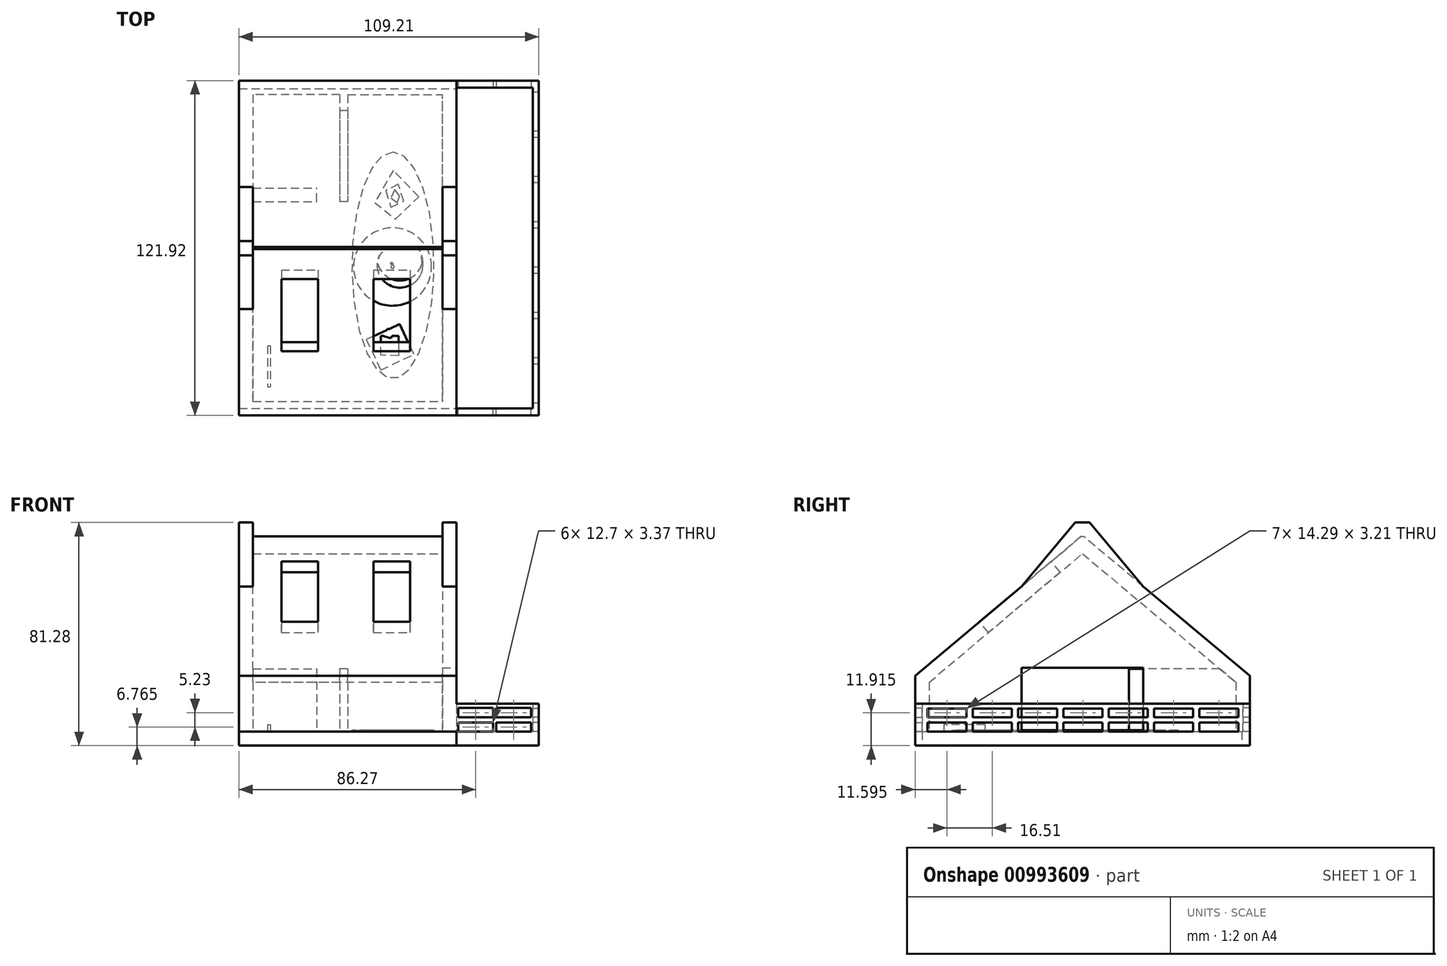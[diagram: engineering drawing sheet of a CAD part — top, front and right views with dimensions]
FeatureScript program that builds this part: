
annotation { "Feature Type Name" : "Feature", "Feature Type Description" : "" }
export const myFeature = defineFeature(function(context is Context, id is Id, definition is map)
    precondition{}
    {
        {
            var Q0;
            Q0=qCreatedBy(makeId("Top.planeOp"),FACE);
            var sketch = newSketch(context, id + "F0", { "sketchPlane" : qUnion([Q0])});
            skLineSegment(sketch, "E0.bottom", {"start": v(-69.71, 93.3) * mm, "end": v(39.5, 93.3) * mm});
            skLineSegment(sketch, "E0.top", {"start": v(-69.71, -28.62) * mm, "end": v(39.5, -28.62) * mm});
            skLineSegment(sketch, "E0.left", {"start": v(-69.71, 93.3) * mm, "end": v(-69.71, -28.62) * mm});
            skLineSegment(sketch, "E0.right", {"start": v(39.5, 93.3) * mm, "end": v(39.5, -28.62) * mm});
            skSolve(sketch);
        }
        {
            var Q0;
            Q0=makeQuery(id+"F0.imprint","IMPRINT",FACE,{"disambiguationData":[TD([[makeQuery(id+"F0.imprint","IMPRINT",EDGE,{"derivedFrom":sQuery(id+"F0.wireOp",EDGE,"E0.bottom")}),-1.0]])]});
            extrude(context, id + "F1", {"entities" : qUnion([Q0]), "depth" : 76.2 * mm, "offsetDistance" : 25.4 * mm});
        }
        {
            var Q0;
            Q0=makeQuery(id+"F1.opExtrude","CAP_FACE",FACE,{"disambiguationData":[OSD([sQuery(id+"F0.wireOp",EDGE,"E0.bottom"),sQuery(id+"F0.wireOp",EDGE,"E0.top"),sQuery(id+"F0.wireOp",EDGE,"E0.left"),sQuery(id+"F0.wireOp",EDGE,"E0.right")])],"isStart":false});
            var sketch = newSketch(context, id + "F2", { "sketchPlane" : qUnion([Q0])});
            skLineSegment(sketch, "E1.right", {"start": v(9.5, -28.62) * mm, "end": v(9.5, 93.3) * mm});
            skLineSegment(sketch, "E2.bottom", {"start": v(9.5, -28.62) * mm, "end": v(39.5, -28.62) * mm});
            skLineSegment(sketch, "E2.top", {"start": v(9.5, 93.3) * mm, "end": v(39.5, 93.3) * mm});
            skLineSegment(sketch, "E2.right", {"start": v(39.5, -28.62) * mm, "end": v(39.5, 93.3) * mm});
            skSolve(sketch);
        }
        {
            var Q0;
            Q0=qSketchRegion(id+"F2",true);
            extrude(context, id + "F3", {"entities" : qUnion([Q0]), "operationType" : NewBodyOperationType.REMOVE, "oppositeDirection" : true, "depth" : 71.12 * mm, "offsetDistance" : 25.4 * mm});
        }
        {
            var Q0;
            Q0=makeQuery(id+"F1.opExtrude","CAP_EDGE",EDGE,{"disambiguationData":[OSD([sQuery(id+"F0.wireOp",EDGE,"E0.bottom")])],"isStart":false});
            var Q1;
            Q1=makeQuery(id+"F1.opExtrude","CAP_EDGE",EDGE,{"disambiguationData":[OSD([sQuery(id+"F0.wireOp",EDGE,"E0.top")])],"isStart":false});
            chamfer(context, id + "F4", {"entities" : qUnion([Q0, Q1]), "chamferType" : ChamferType.OFFSET_ANGLE, "width" : 50.8 * mm, "oppositeDirection" : false, "angle" : 50 * degree, "tangentPropagation" : true});
        }
        {
            var Q0;
            Q0=makeQuery(id+"F3.boolean.opBoolean","COPY",FACE,{"derivedFrom":makeQuery(id+"F3.opExtrude","SWEPT_FACE",FACE,{"disambiguationData":[OSD([sQuery(id+"F2.wireOp",EDGE,"E1.right")])]})});
            var Q1;
            Q1=makeQuery(id+"F1.opExtrude","SWEPT_FACE",FACE,{"disambiguationData":[OSD([sQuery(id+"F0.wireOp",EDGE,"E0.left")])]});
            shell(context, id + "F5", {"entities" : qUnion([Q0, Q1]), "thickness" : 5.08 * mm});
        }
        {
            var Q0;
            Q0=makeQuery(id+"F5.opShell","OFFSET_FACE",FACE,{"disambiguationData":[OSD([sQuery(id+"F0.wireOp",EDGE,"E0.bottom"),sQuery(id+"F0.wireOp",EDGE,"E0.top"),sQuery(id+"F0.wireOp",EDGE,"E0.left"),sQuery(id+"F0.wireOp",EDGE,"E0.right"),sQuery(id+"F2.wireOp",EDGE,"E2.bottom"),sQuery(id+"F2.wireOp",EDGE,"E2.top"),sQuery(id+"F2.wireOp",EDGE,"E1.right"),sQuery(id+"F2.wireOp",EDGE,"E2.right")])]});
            var sketch = newSketch(context, id + "F6", { "sketchPlane" : qUnion([Q0])});
            skPoint(sketch, "E3.oppositeSnap0", {"position": v(9.5, -26.08) * mm});
            skLineSegment(sketch, "E3.bottom", {"start": v(9.5, -28.62) * mm, "end": v(39.5, -28.62) * mm});
            skLineSegment(sketch, "E3.top", {"start": v(9.5, -26.08) * mm, "end": v(39.5, -26.08) * mm});
            skLineSegment(sketch, "E3.left", {"start": v(9.5, -28.62) * mm, "end": v(9.5, -26.08) * mm});
            skLineSegment(sketch, "E3.right", {"start": v(39.5, -28.62) * mm, "end": v(39.5, -26.08) * mm});
            skPoint(sketch, "E4.oppositeSnap0", {"position": v(9.5, 90.76) * mm});
            skLineSegment(sketch, "E4.bottom", {"start": v(9.5, 93.3) * mm, "end": v(39.5, 93.3) * mm});
            skLineSegment(sketch, "E4.top", {"start": v(9.5, 90.76) * mm, "end": v(39.5, 90.76) * mm});
            skLineSegment(sketch, "E4.left", {"start": v(9.5, 93.3) * mm, "end": v(9.5, 90.76) * mm});
            skLineSegment(sketch, "E4.right", {"start": v(39.5, 93.3) * mm, "end": v(39.5, 90.76) * mm});
            skLineSegment(sketch, "E5.bottom", {"start": v(39.5, -28.62) * mm, "end": v(37.37, -28.62) * mm});
            skLineSegment(sketch, "E5.top", {"start": v(39.5, 93.3) * mm, "end": v(37.37, 93.3) * mm});
            skLineSegment(sketch, "E5.left", {"start": v(39.5, -28.62) * mm, "end": v(39.5, 93.3) * mm});
            skLineSegment(sketch, "E5.right", {"start": v(37.37, -28.62) * mm, "end": v(37.37, 93.3) * mm});
            skLineSegment(sketch, "E6.bottom", {"start": v(9.5, -23.54) * mm, "end": v(4.43, -23.54) * mm});
            skLineSegment(sketch, "E6.top", {"start": v(9.5, 88.22) * mm, "end": v(4.43, 88.22) * mm});
            skLineSegment(sketch, "E6.left", {"start": v(9.5, -23.54) * mm, "end": v(9.5, 88.22) * mm});
            skLineSegment(sketch, "E6.right", {"start": v(4.43, -23.54) * mm, "end": v(4.43, 88.22) * mm});
            skLineSegment(sketch, "E7.bottom", {"start": v(-69.71, 88.22) * mm, "end": v(-64.63, 88.22) * mm});
            skLineSegment(sketch, "E7.top", {"start": v(-69.71, -23.54) * mm, "end": v(-64.63, -23.54) * mm});
            skLineSegment(sketch, "E7.left", {"start": v(-69.71, 88.22) * mm, "end": v(-69.71, -23.54) * mm});
            skLineSegment(sketch, "E7.right", {"start": v(-64.63, 88.22) * mm, "end": v(-64.63, -23.54) * mm});
            skLineSegment(sketch, "E8.bottom", {"start": v(-30.1, 88.22) * mm, "end": v(-32.97, 88.22) * mm});
            skLineSegment(sketch, "E8.top", {"start": v(-30.1, 49.23) * mm, "end": v(-32.97, 49.23) * mm});
            skLineSegment(sketch, "E8.left", {"start": v(-30.1, 88.22) * mm, "end": v(-30.1, 49.23) * mm});
            skLineSegment(sketch, "E8.right", {"start": v(-32.97, 88.22) * mm, "end": v(-32.97, 49.23) * mm});
            skLineSegment(sketch, "E9.bottom", {"start": v(-64.63, 49.23) * mm, "end": v(-41.45, 49.23) * mm});
            skLineSegment(sketch, "E9.top", {"start": v(-64.63, 54.2) * mm, "end": v(-41.45, 54.2) * mm});
            skLineSegment(sketch, "E9.left", {"start": v(-64.63, 49.23) * mm, "end": v(-64.63, 54.2) * mm});
            skLineSegment(sketch, "E9.right", {"start": v(-41.45, 49.23) * mm, "end": v(-41.45, 54.2) * mm});
            skEllipse(sketch, "E10", {"center": v(-13.6, 26.06) * mm, "majorRadius": 41.26 * mm, "minorRadius": 14.98 * mm, "majorAxis": v(0, 1)});
            skSolve(sketch);
        }
        {
            var Q0;
            Q0=makeQuery(id+"F6.imprint","IMPRINT",FACE,{"disambiguationData":[TD([[makeQuery(id+"F6.imprint","IMPRINT",EDGE,{"derivedFrom":sQuery(id+"F6.wireOp",EDGE,"E7.bottom")}),-1.0]])]});
            var Q1;
            Q1=makeQuery(id+"F6.imprint","IMPRINT",FACE,{"disambiguationData":[TD([[makeQuery(id+"F6.imprint","IMPRINT",EDGE,{"derivedFrom":sQuery(id+"F6.wireOp",EDGE,"E6.bottom")}),1.0]])]});
            var Q2;
            Q2=qSketchRegion(id+"F9",true);
            extrude(context, id + "F7", {"entities" : qUnion([Q0, Q1, Q2]), "operationType" : NewBodyOperationType.ADD, "depth" : 76.2 * mm, "offsetDistance" : 25.4 * mm});
        }
        {
            var Q0;
            Q0=makeQuery(id+"F7.opExtrude","CAP_EDGE",EDGE,{"disambiguationData":[OSD([sQuery(id+"F6.wireOp",EDGE,"E6.top")])],"isStart":false});
            var Q1;
            Q1=makeQuery(id+"F7.opExtrude","CAP_EDGE",EDGE,{"disambiguationData":[OSD([sQuery(id+"F6.wireOp",EDGE,"E7.bottom")])],"isStart":false});
            var Q2;
            Q2=makeQuery(id+"F7.opExtrude","CAP_EDGE",EDGE,{"disambiguationData":[OSD([sQuery(id+"F6.wireOp",EDGE,"E6.bottom")])],"isStart":false});
            chamfer(context, id + "F8", {"entities" : qUnion([Q0, Q1, Q2]), "chamferType" : ChamferType.OFFSET_ANGLE, "width" : 63.5 * mm, "oppositeDirection" : false, "angle" : 40 * degree});
        }
        {
            var Q0;
            Q0=makeQuery(id+"F7.boolean.opBoolean","MERGE",FACE,{"derivedFrom":[makeQuery(id+"F1.opExtrude","SWEPT_FACE",FACE,{"disambiguationData":[OSD([sQuery(id+"F0.wireOp",EDGE,"E0.left")])]}),makeQuery(id+"F7.opExtrude","SWEPT_FACE",FACE,{"disambiguationData":[OSD([sQuery(id+"F6.wireOp",EDGE,"E7.left")])]})]});
            var sketch = newSketch(context, id + "F9", { "sketchPlane" : qUnion([Q0])});
            skLineSegment(sketch, "E11.0.0", {"start": v(-31.92, 76.2) * mm, "end": v(23.54, 29.66) * mm});
            skLineSegment(sketch, "E11.0.2", {"start": v(23.54, 29.66) * mm, "end": v(28.62, 25.4) * mm});
            skLineSegment(sketch, "E11.0.4", {"start": v(28.62, 25.4) * mm, "end": v(-10.15, 57.94) * mm});
            skLineSegment(sketch, "E11.0.6", {"start": v(-10.15, 57.94) * mm, "end": v(-31.92, 76.2) * mm});
            skLineSegment(sketch, "E12.0.0", {"start": v(-31.92, 76.2) * mm, "end": v(-10.15, 57.94) * mm});
            skLineSegment(sketch, "E12.0.1", {"start": v(-10.15, 57.94) * mm, "end": v(-29.74, 81.28) * mm});
            skLineSegment(sketch, "E12.0.2", {"start": v(-29.74, 81.28) * mm, "end": v(-34.94, 81.28) * mm});
            skLineSegment(sketch, "E12.0.3", {"start": v(-34.94, 81.28) * mm, "end": v(-54.52, 57.94) * mm});
            skLineSegment(sketch, "E12.0.4", {"start": v(-54.52, 57.94) * mm, "end": v(-32.76, 76.2) * mm});
            skLineSegment(sketch, "E12.0.5", {"start": v(-32.76, 76.2) * mm, "end": v(-31.92, 76.2) * mm});
            skLineSegment(sketch, "E13.0.1", {"start": v(-54.52, 57.94) * mm, "end": v(-93.3, 25.4) * mm});
            skLineSegment(sketch, "E13.0.2", {"start": v(-93.3, 25.4) * mm, "end": v(-93.3, 0) * mm});
            skLineSegment(sketch, "E13.0.3", {"start": v(-93.3, 0) * mm, "end": v(28.62, 0) * mm});
            skLineSegment(sketch, "E13.0.4", {"start": v(28.62, 0) * mm, "end": v(28.62, 25.4) * mm});
            skLineSegment(sketch, "E13.0.5", {"start": v(28.62, 25.4) * mm, "end": v(23.54, 29.66) * mm});
            skLineSegment(sketch, "E13.0.6", {"start": v(23.54, 29.66) * mm, "end": v(23.54, 81.28) * mm});
            skLineSegment(sketch, "E13.0.7", {"start": v(23.54, 81.28) * mm, "end": v(-34.94, 81.28) * mm});
            skSolve(sketch);
        }
        {
            var Q0;
            Q0=makeQuery(id+"F9.imprint","IMPRINT",FACE,{"disambiguationData":[TD([[makeQuery(id+"F9.imprint","IMPRINT",EDGE,{"derivedFrom":sQuery(id+"F9.wireOp",EDGE,"E11.0.4")}),-1.0]])]});
            extrude(context, id + "F10", {"entities" : qUnion([Q0]), "operationType" : NewBodyOperationType.REMOVE, "oppositeDirection" : true, "depth" : 25.4 * mm, "offsetDistance" : 25.4 * mm});
        }
        {
            var Q0;
            {var subQ0=sQuery(id+"F6.wireOp",EDGE,"E3.bottom");Q0=makeQuery(id+"F6.imprint","IMPRINT",FACE,{"disambiguationData":[TD([[makeQuery(id+"F6.imprint","IMPRINT",EDGE,{"derivedFrom":subQ0}),1.0]])]});}
            var Q1;
            {var subQ5=sQuery(id+"F6.wireOp",EDGE,"E5.bottom");Q1=makeQuery(id+"F6.imprint","IMPRINT",FACE,{"disambiguationData":[TD([[makeQuery(id+"F6.imprint","IMPRINT",EDGE,{"derivedFrom":subQ5}),1.0]])]});}
            var Q2;
            {var subQ0=sQuery(id+"F6.wireOp",EDGE,"E5.left");var subQ1=sQuery(id+"F6.wireOp",EDGE,"E3.top");var subQ2=makeQuery(id+"F6.imprint","INTERSECT",VERTEX,{"derivedFrom":[subQ1,subQ0]});Q2=makeQuery(id+"F6.imprint","IMPRINT",FACE,{"disambiguationData":[TD([[makeQuery(id+"F6.imprint","IMPRINT",EDGE,{"disambiguationData":[TD([[subQ2,1.0]])],"derivedFrom":subQ1}),1.0]])]});}
            var Q3;
            {var subQ0=sQuery(id+"F6.wireOp",EDGE,"E4.bottom");Q3=makeQuery(id+"F6.imprint","IMPRINT",FACE,{"disambiguationData":[TD([[makeQuery(id+"F6.imprint","IMPRINT",EDGE,{"derivedFrom":subQ0}),-1.0]])]});}
            var Q4;
            {var subQ5=sQuery(id+"F6.wireOp",EDGE,"E5.top");Q4=makeQuery(id+"F6.imprint","IMPRINT",FACE,{"disambiguationData":[TD([[makeQuery(id+"F6.imprint","IMPRINT",EDGE,{"derivedFrom":subQ5}),-1.0]])]});}
            extrude(context, id + "F11", {"entities" : qUnion([Q0, Q1, Q2, Q3, Q4]), "operationType" : NewBodyOperationType.ADD, "depth" : 10.16 * mm, "offsetDistance" : 25.4 * mm});
        }
        {
            var Q0;
            Q0=makeQuery(id+"F11.opExtrude","SWEPT_FACE",FACE,{"disambiguationData":[OSD([sQuery(id+"F6.wireOp",EDGE,"E5.right")])]});
            var sketch = newSketch(context, id + "F12", { "sketchPlane" : qUnion([Q0])});
            skLineSegment(sketch, "E14.bottom", {"start": v(-89.18, 5.08) * mm, "end": v(-74.89, 5.08) * mm});
            skLineSegment(sketch, "E14.top", {"start": v(-89.18, 8.45) * mm, "end": v(-74.89, 8.45) * mm});
            skLineSegment(sketch, "E14.left", {"start": v(-89.18, 5.08) * mm, "end": v(-89.18, 8.45) * mm});
            skLineSegment(sketch, "E14.right", {"start": v(-74.89, 5.08) * mm, "end": v(-74.89, 8.45) * mm});
            skLineSegment(sketch, "E15.bottom", {"start": v(-89.18, 10.31) * mm, "end": v(-74.89, 10.31) * mm});
            skLineSegment(sketch, "E15.top", {"start": v(-89.18, 13.52) * mm, "end": v(-74.89, 13.52) * mm});
            skLineSegment(sketch, "E15.left", {"start": v(-89.18, 10.31) * mm, "end": v(-89.18, 13.52) * mm});
            skLineSegment(sketch, "E15.right", {"start": v(-74.89, 10.31) * mm, "end": v(-74.89, 13.52) * mm});
            skLineSegment(sketch, "E16.1.0.0", {"start": v(-58.38, 5.08) * mm, "end": v(-58.38, 8.45) * mm});
            skLineSegment(sketch, "E16.1.0.1", {"start": v(-72.67, 5.08) * mm, "end": v(-58.38, 5.08) * mm});
            skLineSegment(sketch, "E16.1.0.2", {"start": v(-72.67, 10.31) * mm, "end": v(-72.67, 13.52) * mm});
            skLineSegment(sketch, "E16.1.0.3", {"start": v(-72.67, 10.31) * mm, "end": v(-58.38, 10.31) * mm});
            skLineSegment(sketch, "E16.1.0.4", {"start": v(-58.38, 10.31) * mm, "end": v(-58.38, 13.52) * mm});
            skLineSegment(sketch, "E16.1.0.5", {"start": v(-72.67, 8.45) * mm, "end": v(-58.38, 8.45) * mm});
            skLineSegment(sketch, "E16.1.0.6", {"start": v(-72.67, 13.52) * mm, "end": v(-58.38, 13.52) * mm});
            skLineSegment(sketch, "E16.1.0.7", {"start": v(-72.67, 5.08) * mm, "end": v(-72.67, 8.45) * mm});
            skLineSegment(sketch, "E16.2.0.0", {"start": v(-41.87, 5.08) * mm, "end": v(-41.87, 8.45) * mm});
            skLineSegment(sketch, "E16.2.0.1", {"start": v(-56.16, 5.08) * mm, "end": v(-41.87, 5.08) * mm});
            skLineSegment(sketch, "E16.2.0.2", {"start": v(-56.16, 10.31) * mm, "end": v(-56.16, 13.52) * mm});
            skLineSegment(sketch, "E16.2.0.3", {"start": v(-56.16, 10.31) * mm, "end": v(-41.87, 10.31) * mm});
            skLineSegment(sketch, "E16.2.0.4", {"start": v(-41.87, 10.31) * mm, "end": v(-41.87, 13.52) * mm});
            skLineSegment(sketch, "E16.2.0.5", {"start": v(-56.16, 8.45) * mm, "end": v(-41.87, 8.45) * mm});
            skLineSegment(sketch, "E16.2.0.6", {"start": v(-56.16, 13.52) * mm, "end": v(-41.87, 13.52) * mm});
            skLineSegment(sketch, "E16.2.0.7", {"start": v(-56.16, 5.08) * mm, "end": v(-56.16, 8.45) * mm});
            skLineSegment(sketch, "E16.3.0.0", {"start": v(-25.36, 5.08) * mm, "end": v(-25.36, 8.45) * mm});
            skLineSegment(sketch, "E16.3.0.1", {"start": v(-39.65, 5.08) * mm, "end": v(-25.36, 5.08) * mm});
            skLineSegment(sketch, "E16.3.0.2", {"start": v(-39.65, 10.31) * mm, "end": v(-39.65, 13.52) * mm});
            skLineSegment(sketch, "E16.3.0.3", {"start": v(-39.65, 10.31) * mm, "end": v(-25.36, 10.31) * mm});
            skLineSegment(sketch, "E16.3.0.4", {"start": v(-25.36, 10.31) * mm, "end": v(-25.36, 13.52) * mm});
            skLineSegment(sketch, "E16.3.0.5", {"start": v(-39.65, 8.45) * mm, "end": v(-25.36, 8.45) * mm});
            skLineSegment(sketch, "E16.3.0.6", {"start": v(-39.65, 13.52) * mm, "end": v(-25.36, 13.52) * mm});
            skLineSegment(sketch, "E16.3.0.7", {"start": v(-39.65, 5.08) * mm, "end": v(-39.65, 8.45) * mm});
            skLineSegment(sketch, "E16.4.0.0", {"start": v(-8.85, 5.08) * mm, "end": v(-8.85, 8.45) * mm});
            skLineSegment(sketch, "E16.4.0.1", {"start": v(-23.14, 5.08) * mm, "end": v(-8.85, 5.08) * mm});
            skLineSegment(sketch, "E16.4.0.2", {"start": v(-23.14, 10.31) * mm, "end": v(-23.14, 13.52) * mm});
            skLineSegment(sketch, "E16.4.0.3", {"start": v(-23.14, 10.31) * mm, "end": v(-8.85, 10.31) * mm});
            skLineSegment(sketch, "E16.4.0.4", {"start": v(-8.85, 10.31) * mm, "end": v(-8.85, 13.52) * mm});
            skLineSegment(sketch, "E16.4.0.5", {"start": v(-23.14, 8.45) * mm, "end": v(-8.85, 8.45) * mm});
            skLineSegment(sketch, "E16.4.0.6", {"start": v(-23.14, 13.52) * mm, "end": v(-8.85, 13.52) * mm});
            skLineSegment(sketch, "E16.4.0.7", {"start": v(-23.14, 5.08) * mm, "end": v(-23.14, 8.45) * mm});
            skLineSegment(sketch, "E16.5.0.0", {"start": v(7.66, 5.08) * mm, "end": v(7.66, 8.45) * mm});
            skLineSegment(sketch, "E16.5.0.1", {"start": v(-6.63, 5.08) * mm, "end": v(7.66, 5.08) * mm});
            skLineSegment(sketch, "E16.5.0.2", {"start": v(-6.63, 10.31) * mm, "end": v(-6.63, 13.52) * mm});
            skLineSegment(sketch, "E16.5.0.3", {"start": v(-6.63, 10.31) * mm, "end": v(7.66, 10.31) * mm});
            skLineSegment(sketch, "E16.5.0.4", {"start": v(7.66, 10.31) * mm, "end": v(7.66, 13.52) * mm});
            skLineSegment(sketch, "E16.5.0.5", {"start": v(-6.63, 8.45) * mm, "end": v(7.66, 8.45) * mm});
            skLineSegment(sketch, "E16.5.0.6", {"start": v(-6.63, 13.52) * mm, "end": v(7.66, 13.52) * mm});
            skLineSegment(sketch, "E16.5.0.7", {"start": v(-6.63, 5.08) * mm, "end": v(-6.63, 8.45) * mm});
            skLineSegment(sketch, "E16.6.0.0", {"start": v(24.17, 5.08) * mm, "end": v(24.17, 8.45) * mm});
            skLineSegment(sketch, "E16.6.0.1", {"start": v(9.88, 5.08) * mm, "end": v(24.17, 5.08) * mm});
            skLineSegment(sketch, "E16.6.0.2", {"start": v(9.88, 10.31) * mm, "end": v(9.88, 13.52) * mm});
            skLineSegment(sketch, "E16.6.0.3", {"start": v(9.88, 10.31) * mm, "end": v(24.17, 10.31) * mm});
            skLineSegment(sketch, "E16.6.0.4", {"start": v(24.17, 10.31) * mm, "end": v(24.17, 13.52) * mm});
            skLineSegment(sketch, "E16.6.0.5", {"start": v(9.88, 8.45) * mm, "end": v(24.17, 8.45) * mm});
            skLineSegment(sketch, "E16.6.0.6", {"start": v(9.88, 13.52) * mm, "end": v(24.17, 13.52) * mm});
            skLineSegment(sketch, "E16.6.0.7", {"start": v(9.88, 5.08) * mm, "end": v(9.88, 8.45) * mm});
            skLineSegment(sketch, "E16.direction1", {"start": v(-89.18, 5.08) * mm, "end": v(-72.67, 5.08) * mm, "construction": true});
            skSolve(sketch);
        }
        {
            var Q0;
            Q0=qSketchRegion(id+"F12",true);
            extrude(context, id + "F13", {"entities" : qUnion([Q0]), "operationType" : NewBodyOperationType.REMOVE, "oppositeDirection" : true, "depth" : 5.08 * mm, "offsetDistance" : 25.4 * mm});
        }
        {
            var Q0;
            Q0=makeQuery(id+"F11.opExtrude","SWEPT_FACE",FACE,{"disambiguationData":[OSD([sQuery(id+"F6.wireOp",EDGE,"E3.top")])]});
            var sketch = newSketch(context, id + "F14", { "sketchPlane" : qUnion([Q0])});
            skLineSegment(sketch, "E17.bottom", {"start": v(-36.75, 5.08) * mm, "end": v(-24.05, 5.08) * mm});
            skLineSegment(sketch, "E17.top", {"start": v(-36.75, 8.45) * mm, "end": v(-24.05, 8.45) * mm});
            skLineSegment(sketch, "E17.left", {"start": v(-36.75, 5.08) * mm, "end": v(-36.75, 8.45) * mm});
            skLineSegment(sketch, "E17.right", {"start": v(-24.05, 5.08) * mm, "end": v(-24.05, 8.45) * mm});
            skLineSegment(sketch, "E18.0.1.0", {"start": v(-24.05, 10.31) * mm, "end": v(-24.05, 13.68) * mm});
            skLineSegment(sketch, "E18.0.1.1", {"start": v(-36.75, 13.68) * mm, "end": v(-24.05, 13.68) * mm});
            skLineSegment(sketch, "E18.0.1.2", {"start": v(-36.75, 10.31) * mm, "end": v(-24.05, 10.31) * mm});
            skLineSegment(sketch, "E18.0.1.3", {"start": v(-36.75, 10.31) * mm, "end": v(-36.75, 13.68) * mm});
            skLineSegment(sketch, "E18.1.0.0", {"start": v(-10.23, 5.08) * mm, "end": v(-10.23, 8.45) * mm});
            skLineSegment(sketch, "E18.1.0.1", {"start": v(-22.93, 8.45) * mm, "end": v(-10.23, 8.45) * mm});
            skLineSegment(sketch, "E18.1.0.2", {"start": v(-22.93, 5.08) * mm, "end": v(-10.23, 5.08) * mm});
            skLineSegment(sketch, "E18.1.0.3", {"start": v(-22.93, 5.08) * mm, "end": v(-22.93, 8.45) * mm});
            skLineSegment(sketch, "E18.1.1.0", {"start": v(-10.23, 10.31) * mm, "end": v(-10.23, 13.68) * mm});
            skLineSegment(sketch, "E18.1.1.1", {"start": v(-22.93, 13.68) * mm, "end": v(-10.23, 13.68) * mm});
            skLineSegment(sketch, "E18.1.1.2", {"start": v(-22.93, 10.31) * mm, "end": v(-10.23, 10.31) * mm});
            skLineSegment(sketch, "E18.1.1.3", {"start": v(-22.93, 10.31) * mm, "end": v(-22.93, 13.68) * mm});
            skLineSegment(sketch, "E18.direction1", {"start": v(-36.75, 5.08) * mm, "end": v(-22.93, 5.08) * mm, "construction": true});
            skLineSegment(sketch, "E18.direction2", {"start": v(-36.75, 5.08) * mm, "end": v(-36.75, 10.31) * mm, "construction": true});
            skSolve(sketch);
        }
        {
            var Q0;
            Q0=qSketchRegion(id+"F14",true);
            extrude(context, id + "F15", {"entities" : qUnion([Q0]), "operationType" : NewBodyOperationType.REMOVE, "oppositeDirection" : true, "depth" : 5.08 * mm, "offsetDistance" : 25.4 * mm});
        }
        {
            var Q0;
            Q0=makeQuery(id+"F11.opExtrude","SWEPT_FACE",FACE,{"disambiguationData":[OSD([sQuery(id+"F6.wireOp",EDGE,"E4.top")])]});
            var sketch = newSketch(context, id + "F16", { "sketchPlane" : qUnion([Q0])});
            skLineSegment(sketch, "E19.bottom", {"start": v(10.21, 5.08) * mm, "end": v(22.91, 5.08) * mm});
            skLineSegment(sketch, "E19.top", {"start": v(10.21, 8.45) * mm, "end": v(22.91, 8.45) * mm});
            skLineSegment(sketch, "E19.left", {"start": v(10.21, 5.08) * mm, "end": v(10.21, 8.45) * mm});
            skLineSegment(sketch, "E19.right", {"start": v(22.91, 5.08) * mm, "end": v(22.91, 8.45) * mm});
            skLineSegment(sketch, "E20.0.1.0", {"start": v(22.91, 10.31) * mm, "end": v(22.91, 13.68) * mm});
            skLineSegment(sketch, "E20.0.1.1", {"start": v(10.21, 13.68) * mm, "end": v(22.91, 13.68) * mm});
            skLineSegment(sketch, "E20.0.1.2", {"start": v(10.21, 10.31) * mm, "end": v(22.91, 10.31) * mm});
            skLineSegment(sketch, "E20.0.1.3", {"start": v(10.21, 10.31) * mm, "end": v(10.21, 13.68) * mm});
            skLineSegment(sketch, "E20.1.0.0", {"start": v(36.73, 5.08) * mm, "end": v(36.73, 8.45) * mm});
            skLineSegment(sketch, "E20.1.0.1", {"start": v(24.03, 8.45) * mm, "end": v(36.73, 8.45) * mm});
            skLineSegment(sketch, "E20.1.0.2", {"start": v(24.03, 5.08) * mm, "end": v(36.73, 5.08) * mm});
            skLineSegment(sketch, "E20.1.0.3", {"start": v(24.03, 5.08) * mm, "end": v(24.03, 8.45) * mm});
            skLineSegment(sketch, "E20.1.1.0", {"start": v(36.73, 10.31) * mm, "end": v(36.73, 13.68) * mm});
            skLineSegment(sketch, "E20.1.1.1", {"start": v(24.03, 13.68) * mm, "end": v(36.73, 13.68) * mm});
            skLineSegment(sketch, "E20.1.1.2", {"start": v(24.03, 10.31) * mm, "end": v(36.73, 10.31) * mm});
            skLineSegment(sketch, "E20.1.1.3", {"start": v(24.03, 10.31) * mm, "end": v(24.03, 13.68) * mm});
            skLineSegment(sketch, "E20.direction1", {"start": v(10.21, 5.08) * mm, "end": v(24.03, 5.08) * mm, "construction": true});
            skLineSegment(sketch, "E20.direction2", {"start": v(10.21, 5.08) * mm, "end": v(10.21, 10.31) * mm, "construction": true});
            skSolve(sketch);
        }
        {
            var Q0;
            Q0=qSketchRegion(id+"F16",true);
            extrude(context, id + "F17", {"entities" : qUnion([Q0]), "operationType" : NewBodyOperationType.REMOVE, "oppositeDirection" : true, "depth" : 5.08 * mm, "offsetDistance" : 25.4 * mm});
        }
        {
            var Q0;
            Q0=makeQuery(id+"F7.boolean.opBoolean","MERGE",FACE,{"derivedFrom":[makeQuery(id+"F3.boolean.opBoolean","COPY",FACE,{"derivedFrom":makeQuery(id+"F3.opExtrude","SWEPT_FACE",FACE,{"disambiguationData":[OSD([sQuery(id+"F2.wireOp",EDGE,"E1.right")])]})}),makeQuery(id+"F7.opExtrude","SWEPT_FACE",FACE,{"disambiguationData":[OSD([sQuery(id+"F6.wireOp",EDGE,"E6.left")])]})]});
            var sketch = newSketch(context, id + "F18", { "sketchPlane" : qUnion([Q0])});
            skLineSegment(sketch, "E21.bottom", {"start": v(10.15, 28.35) * mm, "end": v(54.52, 28.35) * mm});
            skLineSegment(sketch, "E21.top", {"start": v(10.15, 5.08) * mm, "end": v(54.52, 5.08) * mm});
            skLineSegment(sketch, "E21.left", {"start": v(10.15, 28.35) * mm, "end": v(10.15, 5.08) * mm});
            skLineSegment(sketch, "E21.right", {"start": v(54.52, 28.35) * mm, "end": v(54.52, 5.08) * mm});
            skSolve(sketch);
        }
        {
            var Q0;
            Q0=makeQuery(id+"F18.imprint","IMPRINT",FACE,{"disambiguationData":[TD([[makeQuery(id+"F18.imprint","IMPRINT",EDGE,{"derivedFrom":sQuery(id+"F18.wireOp",EDGE,"E21.bottom")}),-1.0]])]});
            extrude(context, id + "F19", {"entities" : qUnion([Q0]), "operationType" : NewBodyOperationType.REMOVE, "oppositeDirection" : true, "depth" : 5.08 * mm, "offsetDistance" : 25.4 * mm});
        }
        {
            var Q0;
            Q0=makeQuery(id+"F10.boolean.opBoolean","MERGE",FACE,{"derivedFrom":[makeQuery(id+"F4.opChamfer","BLEND_FACE",FACE,{"disambiguationData":[OSD([sQuery(id+"F0.wireOp",EDGE,"E0.top")])]})],"fromTools":[makeQuery(id+"F10.opExtrude","SWEPT_FACE",FACE,{"disambiguationData":[OSD([sQuery(id+"F9.wireOp",EDGE,"E11.0.4")])]})]});
            var sketch = newSketch(context, id + "F20", { "sketchPlane" : qUnion([Q0])});
            skPoint(sketch, "E22.firstSnap0", {"position": v(-64.63, 59.23) * mm});
            skLineSegment(sketch, "E22.bottom", {"start": v(-54.26, 59.23) * mm, "end": v(-40.94, 59.23) * mm});
            skLineSegment(sketch, "E22.top", {"start": v(-54.26, 25) * mm, "end": v(-40.94, 25) * mm});
            skLineSegment(sketch, "E22.left", {"start": v(-54.26, 59.23) * mm, "end": v(-54.26, 25) * mm});
            skLineSegment(sketch, "E22.right", {"start": v(-40.94, 59.23) * mm, "end": v(-40.94, 25) * mm});
            skLineSegment(sketch, "E23.1.0.0", {"start": v(-20.74, 25) * mm, "end": v(-7.41, 25) * mm});
            skLineSegment(sketch, "E23.1.0.1", {"start": v(-7.41, 59.23) * mm, "end": v(-7.41, 25) * mm});
            skLineSegment(sketch, "E23.1.0.2", {"start": v(-20.74, 59.23) * mm, "end": v(-20.74, 25) * mm});
            skLineSegment(sketch, "E23.1.0.3", {"start": v(-20.74, 59.23) * mm, "end": v(-7.41, 59.23) * mm});
            skLineSegment(sketch, "E23.direction1", {"start": v(-54.26, 25) * mm, "end": v(-20.74, 25) * mm, "construction": true});
            skSolve(sketch);
        }
        {
            var Q0;
            Q0=qSketchRegion(id+"F20",true);
            extrude(context, id + "F21", {"entities" : qUnion([Q0]), "operationType" : NewBodyOperationType.REMOVE, "oppositeDirection" : true, "depth" : 5.08 * mm, "offsetDistance" : 25.4 * mm});
        }
        {
            var Q0;
            Q0=makeQuery(id+"F6.imprint","IMPRINT",FACE,{"disambiguationData":[TD([[makeQuery(id+"F6.imprint","IMPRINT",EDGE,{"derivedFrom":sQuery(id+"F6.wireOp",EDGE,"E9.bottom")}),1.0]])]});
            var Q1;
            Q1=makeQuery(id+"F6.imprint","IMPRINT",FACE,{"disambiguationData":[TD([[makeQuery(id+"F6.imprint","IMPRINT",EDGE,{"derivedFrom":sQuery(id+"F6.wireOp",EDGE,"E8.bottom")}),-1.0]])]});
            extrude(context, id + "F22", {"entities" : qUnion([Q0, Q1]), "operationType" : NewBodyOperationType.ADD, "depth" : 22.86 * mm, "offsetDistance" : 25.4 * mm});
        }
        {
            var Q0;
            Q0=makeQuery(id+"F6.imprint","IMPRINT",FACE,{"disambiguationData":[TD([[makeQuery(id+"F6.imprint","IMPRINT",EDGE,{"derivedFrom":sQuery(id+"F6.wireOp",EDGE,"E10")}),1.0]])]});
            extrude(context, id + "F23", {"entities" : qUnion([Q0]), "operationType" : NewBodyOperationType.ADD, "depth" : 0.25 * mm, "offsetDistance" : 25.4 * mm});
        }
        {
            var Q0;
            Q0=makeQuery(id+"F23.opExtrude","CAP_FACE",FACE,{"disambiguationData":[OSD([sQuery(id+"F6.wireOp",EDGE,"E10")])],"isStart":false});
            var sketch = newSketch(context, id + "F24", { "sketchPlane" : qUnion([Q0])});
            skArc(sketch, "E24", {"start": v(-13.6, 26.06) * mm, "mid": v(-13.87, 26.97) * mm, "end": v(-14.62, 26.38) * mm});
            skArc(sketch, "E25", {"start": v(-14.62, 26.38) * mm, "mid": v(-10.97, 22.3) * mm, "end": v(-7.32, 26.38) * mm});
            skArc(sketch, "E26", {"start": v(-7.32, 26.38) * mm, "mid": v(-13.2, 32.68) * mm, "end": v(-19.07, 26.38) * mm});
            skArc(sketch, "E27", {"start": v(-19.07, 26.38) * mm, "mid": v(-11.07, 20.51) * mm, "end": v(-3.1, 26.42) * mm});
            skArc(sketch, "E28", {"start": v(-3.1, 26.42) * mm, "mid": v(-13.68, 37.98) * mm, "end": v(-24.25, 26.42) * mm});
            skArc(sketch, "E29", {"start": v(-13.92, 26.06) * mm, "mid": v(-13.76, 24.94) * mm, "end": v(-13.6, 26.06) * mm});
            skArc(sketch, "E30", {"start": v(-13.92, 26.06) * mm, "mid": v(-14.36, 26.55) * mm, "end": v(-14.8, 26.06) * mm});
            skArc(sketch, "E31", {"start": v(-14.8, 26.06) * mm, "mid": v(-11.93, 22.8) * mm, "end": v(-8.47, 25.42) * mm});
            skArc(sketch, "E32", {"start": v(-8.47, 25.42) * mm, "mid": v(-13.7, 32.14) * mm, "end": v(-19.4, 25.8) * mm});
            skArc(sketch, "E33", {"start": v(-19.4, 25.8) * mm, "mid": v(-10.54, 17.92) * mm, "end": v(-2.66, 26.8) * mm});
            skArc(sketch, "E34", {"start": v(-2.66, 26.8) * mm, "mid": v(-13.64, 37.4) * mm, "end": v(-24.25, 26.42) * mm});
            skCircle(sketch, "E35", {"center": v(-13.76, 25.52) * mm, "radius": 14.2 * mm});
            skLineSegment(sketch, "E36", {"start": v(-23.35, -0.92) * mm, "end": v(-18.02, -12.09) * mm});
            skLineSegment(sketch, "E37", {"start": v(-18.02, -12.09) * mm, "end": v(-5.98, -6.35) * mm});
            skLineSegment(sketch, "E38", {"start": v(-5.98, -6.35) * mm, "end": v(-11.2, 4.6) * mm});
            skLineSegment(sketch, "E39", {"start": v(-11.2, 4.6) * mm, "end": v(-23.35, -0.92) * mm});
            skLineSegment(sketch, "E40", {"start": v(-18.07, -6.7) * mm, "end": v(-18.07, 0.38) * mm});
            skLineSegment(sketch, "E41", {"start": v(-18.07, 0.38) * mm, "end": v(-11.56, 0.38) * mm});
            skLineSegment(sketch, "E42", {"start": v(-11.56, 0.38) * mm, "end": v(-11.56, -6.92) * mm});
            skLineSegment(sketch, "E43", {"start": v(-11.56, -6.92) * mm, "end": v(-18.07, -6.7) * mm});
            skLineSegment(sketch, "E44", {"start": v(-16.93, 0.19) * mm, "end": v(-14.35, -0.53) * mm});
            skLineSegment(sketch, "E45", {"start": v(-14.35, -0.53) * mm, "end": v(-13.24, 1.97) * mm});
            skLineSegment(sketch, "E46", {"start": v(-13.24, 1.97) * mm, "end": v(-15.56, 3) * mm});
            skLineSegment(sketch, "E47", {"start": v(-15.56, 3) * mm, "end": v(-16.93, 0.19) * mm});
            skLineSegment(sketch, "E48", {"start": v(-20.23, 48.91) * mm, "end": v(-12.74, 42.9) * mm});
            skLineSegment(sketch, "E49", {"start": v(-12.74, 42.9) * mm, "end": v(-4.23, 50.98) * mm});
            skLineSegment(sketch, "E50", {"start": v(-4.23, 50.98) * mm, "end": v(-13.44, 60.67) * mm});
            skLineSegment(sketch, "E51", {"start": v(-13.44, 60.67) * mm, "end": v(-20.23, 48.91) * mm});
            skLineSegment(sketch, "E52", {"start": v(-16.2, 53.3) * mm, "end": v(-14.36, 47.22) * mm});
            skLineSegment(sketch, "E53", {"start": v(-14.36, 47.22) * mm, "end": v(-9.67, 49.46) * mm});
            skLineSegment(sketch, "E54", {"start": v(-9.67, 49.46) * mm, "end": v(-11.66, 55.6) * mm});
            skLineSegment(sketch, "E55", {"start": v(-11.66, 55.6) * mm, "end": v(-16.2, 53.3) * mm});
            skLineSegment(sketch, "E56", {"start": v(-14.36, 50.6) * mm, "end": v(-12.01, 48.91) * mm});
            skPoint(sketch, "E56.endSnap0", {"position": v(-12.01, 48.34) * mm});
            skLineSegment(sketch, "E57", {"start": v(-12.01, 48.91) * mm, "end": v(-11.19, 51.29) * mm});
            skLineSegment(sketch, "E58", {"start": v(-11.19, 51.29) * mm, "end": v(-12.99, 53.67) * mm});
            skLineSegment(sketch, "E59", {"start": v(-12.99, 53.67) * mm, "end": v(-14.36, 50.6) * mm});
            skSolve(sketch);
        }
        {
            var Q0;
            Q0=makeQuery(id+"F24.imprint","IMPRINT",FACE,{"disambiguationData":[TD([[makeQuery(id+"F24.imprint","IMPRINT",EDGE,{"derivedFrom":sQuery(id+"F24.wireOp",EDGE,"E24")}),1.0]])]});
            var Q1;
            Q1=makeQuery(id+"F24.imprint","IMPRINT",FACE,{"disambiguationData":[TD([[makeQuery(id+"F24.imprint","IMPRINT",EDGE,{"derivedFrom":sQuery(id+"F24.wireOp",EDGE,"E35")}),-1.0]])]});
            var Q2;
            Q2=makeQuery(id+"F24.imprint","IMPRINT",FACE,{"disambiguationData":[TD([[makeQuery(id+"F24.imprint","IMPRINT",EDGE,{"derivedFrom":sQuery(id+"F24.wireOp",EDGE,"E40")}),-1.0]])]});
            var Q3;
            Q3=makeQuery(id+"F24.imprint","IMPRINT",FACE,{"disambiguationData":[TD([[makeQuery(id+"F24.imprint","IMPRINT",EDGE,{"derivedFrom":sQuery(id+"F24.wireOp",EDGE,"E52")}),1.0]])]});
            var Q4;
            {var subQ1=sQuery(id+"F24.wireOp",EDGE,"E27");Q4=makeQuery(id+"F24.imprint","IMPRINT",FACE,{"disambiguationData":[TD([[makeQuery(id+"F24.imprint","IMPRINT",EDGE,{"derivedFrom":subQ1}),-1.0]])]});}
            extrude(context, id + "F25", {"entities" : qUnion([Q0, Q1, Q2, Q3, Q4]), "operationType" : NewBodyOperationType.ADD, "depth" : 0.25 * mm, "offsetDistance" : 25.4 * mm});
        }
        {
            var Q0;
            {var subQ4=sQuery(id+"F6.wireOp",EDGE,"E6.right");Q0=makeQuery(id+"F6.imprint","IMPRINT",FACE,{"disambiguationData":[TD([[makeQuery(id+"F6.imprint","IMPRINT",EDGE,{"derivedFrom":subQ4}),1.0]])]});}
            var sketch = newSketch(context, id + "F26", { "sketchPlane" : qUnion([Q0])});
            skLineSegment(sketch, "E60.bottom", {"start": v(-59.26, -3.22) * mm, "end": v(-58.23, -3.22) * mm});
            skLineSegment(sketch, "E60.top", {"start": v(-59.26, -18.15) * mm, "end": v(-58.23, -18.15) * mm});
            skLineSegment(sketch, "E60.left", {"start": v(-59.26, -3.22) * mm, "end": v(-59.26, -18.15) * mm});
            skLineSegment(sketch, "E60.right", {"start": v(-58.23, -3.22) * mm, "end": v(-58.23, -18.15) * mm});
            skSolve(sketch);
        }
        {
            var Q0;
            {var subQ0=sQuery(id+"F26.wireOp",EDGE,"E60.bottom");Q0=makeQuery(id+"F26.imprint","IMPRINT",FACE,{"disambiguationData":[TD([[makeQuery(id+"F26.imprint","IMPRINT",EDGE,{"derivedFrom":subQ0}),-1.0]])]});}
            extrude(context, id + "F27", {"entities" : qUnion([Q0]), "operationType" : NewBodyOperationType.ADD, "depth" : 2.54 * mm, "offsetDistance" : 25.4 * mm});
        }
        {
            var Q0;
            Q0=makeQuery(id+"F1.opExtrude","CAP_FACE",FACE,{"disambiguationData":[OSD([sQuery(id+"F0.wireOp",EDGE,"E0.bottom"),sQuery(id+"F0.wireOp",EDGE,"E0.top"),sQuery(id+"F0.wireOp",EDGE,"E0.left"),sQuery(id+"F0.wireOp",EDGE,"E0.right")])],"isStart":true});
            var sketch = newSketch(context, id + "F28", { "sketchPlane" : qUnion([Q0])});
            skLineSegment(sketch, "E61.bottom", {"start": v(-69.71, 28.62) * mm, "end": v(9.5, 28.62) * mm});
            skLineSegment(sketch, "E61.top", {"start": v(-69.71, 26.09) * mm, "end": v(9.5, 26.09) * mm});
            skLineSegment(sketch, "E61.left", {"start": v(-69.71, 28.62) * mm, "end": v(-69.71, 26.09) * mm});
            skLineSegment(sketch, "E61.right", {"start": v(9.5, 28.62) * mm, "end": v(9.5, 26.09) * mm});
            skLineSegment(sketch, "E62.bottom", {"start": v(-69.71, -93.3) * mm, "end": v(9.5, -93.3) * mm});
            skLineSegment(sketch, "E62.top", {"start": v(-69.71, -90.39) * mm, "end": v(9.5, -90.39) * mm});
            skLineSegment(sketch, "E62.left", {"start": v(-69.71, -93.3) * mm, "end": v(-69.71, -90.39) * mm});
            skLineSegment(sketch, "E62.right", {"start": v(9.5, -93.3) * mm, "end": v(9.5, -90.39) * mm});
            skSolve(sketch);
        }
        {
            var Q0;
            Q0=makeQuery(id+"F28.imprint","IMPRINT",FACE,{"disambiguationData":[TD([[makeQuery(id+"F28.imprint","IMPRINT",EDGE,{"derivedFrom":sQuery(id+"F28.wireOp",EDGE,"E61.bottom")}),-1.0]])]});
            var Q1;
            Q1=makeQuery(id+"F28.imprint","IMPRINT",FACE,{"disambiguationData":[TD([[makeQuery(id+"F28.imprint","IMPRINT",EDGE,{"derivedFrom":sQuery(id+"F28.wireOp",EDGE,"E62.bottom")}),1.0]])]});
            extrude(context, id + "F29", {"entities" : qUnion([Q0, Q1]), "operationType" : NewBodyOperationType.REMOVE, "oppositeDirection" : true, "depth" : 5.05 * mm, "offsetDistance" : 25.4 * mm});
        }
    });
